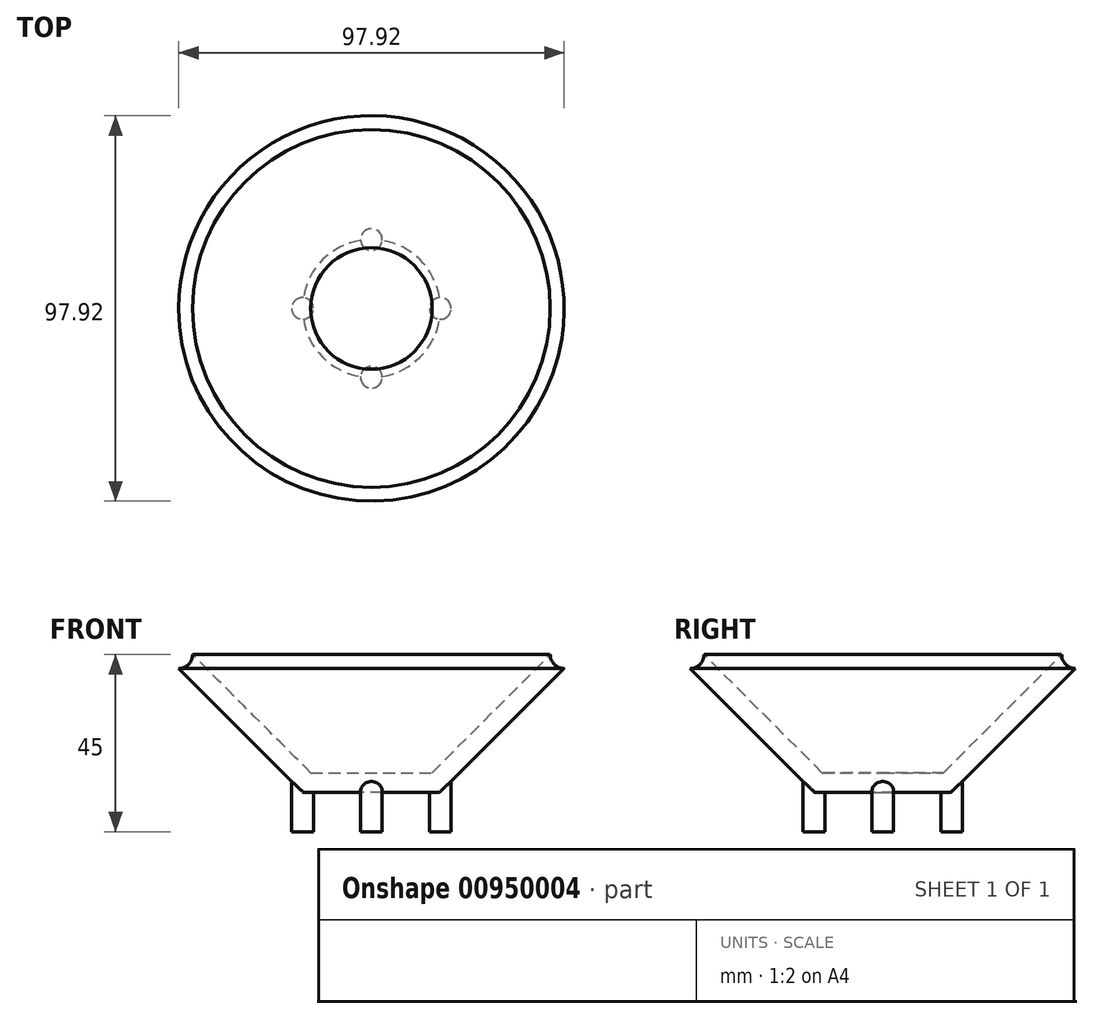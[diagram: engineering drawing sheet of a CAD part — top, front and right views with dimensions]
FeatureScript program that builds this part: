
annotation { "Feature Type Name" : "Feature", "Feature Type Description" : "" }
export const myFeature = defineFeature(function(context is Context, id is Id, definition is map)
    precondition{}
    {
        {
            var Q0;
            Q0=qCreatedBy(makeId("Front.planeOp"),FACE);
            var sketch = newSketch(context, id + "F0", { "sketchPlane" : qUnion([Q0])});
            skLineSegment(sketch, "E0", {"start": v(0, 0) * mm, "end": v(0, 35) * mm, "construction": true});
            skLineSegment(sketch, "E1", {"start": v(0, 0) * mm, "end": v(17.5, 0) * mm});
            skLineSegment(sketch, "E2", {"start": v(17.5, 0) * mm, "end": v(52.5, 35) * mm});
            skLineSegment(sketch, "E3.0", {"start": v(15.43, 5) * mm, "end": v(45.43, 35) * mm});
            skLineSegment(sketch, "E3.1", {"start": v(0, 5) * mm, "end": v(15.43, 5) * mm});
            skLineSegment(sketch, "E4", {"start": v(0, 5) * mm, "end": v(0, 0) * mm});
            skLineSegment(sketch, "E5", {"start": v(45.43, 35) * mm, "end": v(52.5, 35) * mm});
            skCircle(sketch, "E6", {"center": v(48.96, 35) * mm, "radius": 3.54 * mm});
            skPoint(sketch, "E6.centerSnap0", {"position": v(48.96, 35) * mm});
            skLineSegment(sketch, "E7", {"start": v(52.5, 35) * mm, "end": v(45.43, 35) * mm});
            skSolve(sketch);
        }
        {
            var Q0;
            {var subQ2=sQuery(id+"F0.wireOp",EDGE,"E1");Q0=makeQuery(id+"F0.imprint","IMPRINT",FACE,{"disambiguationData":[TD([[makeQuery(id+"F0.imprint","IMPRINT",EDGE,{"derivedFrom":subQ2}),1.0]])]});}
            var Q1;
            {var subQ0=sQuery(id+"F0.wireOp",EDGE,"E7");Q1=makeQuery(id+"F0.imprint","IMPRINT",FACE,{"disambiguationData":[TD([[makeQuery(id+"F0.imprint","IMPRINT",EDGE,{"derivedFrom":subQ0}),-1.0]])]});}
            var Q2;
            {var subQ0=sQuery(id+"F0.wireOp",EDGE,"E7");Q2=makeQuery(id+"F0.imprint","IMPRINT",FACE,{"disambiguationData":[TD([[makeQuery(id+"F0.imprint","IMPRINT",EDGE,{"derivedFrom":subQ0}),1.0]])]});}
            var Q3;
            Q3=sQuery(id+"F0.wireOp",EDGE,"E0");
            revolve(context, id + "F1", {"surfaceOperationType" : NewSurfaceOperationType.NEW, "entities" : qUnion([Q0, Q1, Q2]), "axis" : qUnion([Q3]), "revolveType" : RevolveType.FULL});
        }
        {
            var Q0;
            Q0=makeQuery(id+"F1.opRevolve","SWEPT_FACE",FACE,{"disambiguationData":[OSD([sQuery(id+"F0.wireOp",EDGE,"E1")])]});
            var sketch = newSketch(context, id + "F2", { "sketchPlane" : qUnion([Q0])});
            skLineSegment(sketch, "E8", {"start": v(-50.3, 0) * mm, "end": v(49.89, 0) * mm, "construction": true});
            skLineSegment(sketch, "E9", {"start": v(0, 49.68) * mm, "end": v(0, -50.5) * mm, "construction": true});
            skCircle(sketch, "E10", {"center": v(17.5, 0) * mm, "radius": 2.75 * mm});
            skCircle(sketch, "E11", {"center": v(0, 17.5) * mm, "radius": 2.75 * mm});
            skCircle(sketch, "E12", {"center": v(-17.5, 0) * mm, "radius": 2.75 * mm});
            skCircle(sketch, "E13", {"center": v(0, -17.5) * mm, "radius": 2.75 * mm});
            skSolve(sketch);
        }
        {
            var Q0;
            {var subQ0=sQuery(id+"F2.wireOp",EDGE,"E12");var subQ1=makeQuery(id+"F1.opRevolve","SWEPT_EDGE",EDGE,{"disambiguationData":[OSD([sQuery(id+"F0.wireOp",EDGE,"E1"),sQuery(id+"F0.wireOp",EDGE,"E2")])]});var subQ2=makeQuery(id+"F2.imprint","INTERSECT",VERTEX,{"disambiguationData":[OD(0.0)],"derivedFrom":[subQ1,subQ0]});Q0=makeQuery(id+"F2.imprint","IMPRINT",FACE,{"disambiguationData":[TD([[makeQuery(id+"F2.imprint","IMPRINT",EDGE,{"disambiguationData":[TD([[subQ2,-1.0]])],"derivedFrom":subQ0}),1.0]])]});}
            var Q1;
            {var subQ0=sQuery(id+"F2.wireOp",EDGE,"E11");var subQ1=makeQuery(id+"F1.opRevolve","SWEPT_EDGE",EDGE,{"disambiguationData":[OSD([sQuery(id+"F0.wireOp",EDGE,"E1"),sQuery(id+"F0.wireOp",EDGE,"E2")])]});var subQ2=makeQuery(id+"F2.imprint","INTERSECT",VERTEX,{"disambiguationData":[OD(0.0)],"derivedFrom":[subQ1,subQ0]});Q1=makeQuery(id+"F2.imprint","IMPRINT",FACE,{"disambiguationData":[TD([[makeQuery(id+"F2.imprint","IMPRINT",EDGE,{"disambiguationData":[TD([[subQ2,1.0]])],"derivedFrom":subQ0}),1.0]])]});}
            var Q2;
            {var subQ0=sQuery(id+"F2.wireOp",EDGE,"E13");var subQ1=makeQuery(id+"F1.opRevolve","SWEPT_EDGE",EDGE,{"disambiguationData":[OSD([sQuery(id+"F0.wireOp",EDGE,"E1"),sQuery(id+"F0.wireOp",EDGE,"E2")])]});var subQ2=makeQuery(id+"F2.imprint","INTERSECT",VERTEX,{"disambiguationData":[OD(0.0)],"derivedFrom":[subQ1,subQ0]});Q2=makeQuery(id+"F2.imprint","IMPRINT",FACE,{"disambiguationData":[TD([[makeQuery(id+"F2.imprint","IMPRINT",EDGE,{"disambiguationData":[TD([[subQ2,-1.0]])],"derivedFrom":subQ0}),1.0]])]});}
            var Q3;
            {var subQ0=sQuery(id+"F2.wireOp",EDGE,"E10");var subQ1=makeQuery(id+"F1.opRevolve","SWEPT_EDGE",EDGE,{"disambiguationData":[OSD([sQuery(id+"F0.wireOp",EDGE,"E1"),sQuery(id+"F0.wireOp",EDGE,"E2")])]});var subQ2=makeQuery(id+"F2.imprint","INTERSECT",VERTEX,{"disambiguationData":[OD(0.0)],"derivedFrom":[subQ1,subQ0]});Q3=makeQuery(id+"F2.imprint","IMPRINT",FACE,{"disambiguationData":[TD([[makeQuery(id+"F2.imprint","IMPRINT",EDGE,{"disambiguationData":[TD([[subQ2,1.0]])],"derivedFrom":subQ0}),1.0]])]});}
            extrude(context, id + "F3", {"entities" : qUnion([Q0, Q1, Q2, Q3]), "operationType" : NewBodyOperationType.ADD, "endBound" : BoundingType.UP_TO_NEXT, "oppositeDirection" : true, "depth" : 25 * mm, "offsetDistance" : 25 * mm});
        }
        {
            var Q0;
            {var subQ0=sQuery(id+"F2.wireOp",EDGE,"E10");var subQ1=makeQuery(id+"F1.opRevolve","SWEPT_EDGE",EDGE,{"disambiguationData":[OSD([sQuery(id+"F0.wireOp",EDGE,"E1"),sQuery(id+"F0.wireOp",EDGE,"E2")])]});var subQ2=makeQuery(id+"F2.imprint","INTERSECT",VERTEX,{"disambiguationData":[OD(0.0)],"derivedFrom":[subQ1,subQ0]});Q0=makeQuery(id+"F2.imprint","IMPRINT",FACE,{"disambiguationData":[TD([[makeQuery(id+"F2.imprint","IMPRINT",EDGE,{"disambiguationData":[TD([[subQ2,1.0]])],"derivedFrom":subQ0}),1.0]])]});}
            var Q1;
            {var subQ0=sQuery(id+"F2.wireOp",EDGE,"E11");var subQ1=makeQuery(id+"F1.opRevolve","SWEPT_EDGE",EDGE,{"disambiguationData":[OSD([sQuery(id+"F0.wireOp",EDGE,"E1"),sQuery(id+"F0.wireOp",EDGE,"E2")])]});var subQ2=makeQuery(id+"F2.imprint","INTERSECT",VERTEX,{"disambiguationData":[OD(0.0)],"derivedFrom":[subQ1,subQ0]});Q1=makeQuery(id+"F2.imprint","IMPRINT",FACE,{"disambiguationData":[TD([[makeQuery(id+"F2.imprint","IMPRINT",EDGE,{"disambiguationData":[TD([[subQ2,1.0]])],"derivedFrom":subQ0}),1.0]])]});}
            var Q2;
            {var subQ0=sQuery(id+"F2.wireOp",EDGE,"E12");var subQ1=makeQuery(id+"F1.opRevolve","SWEPT_EDGE",EDGE,{"disambiguationData":[OSD([sQuery(id+"F0.wireOp",EDGE,"E1"),sQuery(id+"F0.wireOp",EDGE,"E2")])]});var subQ2=makeQuery(id+"F2.imprint","INTERSECT",VERTEX,{"disambiguationData":[OD(0.0)],"derivedFrom":[subQ1,subQ0]});Q2=makeQuery(id+"F2.imprint","IMPRINT",FACE,{"disambiguationData":[TD([[makeQuery(id+"F2.imprint","IMPRINT",EDGE,{"disambiguationData":[TD([[subQ2,-1.0]])],"derivedFrom":subQ0}),1.0]])]});}
            var Q3;
            {var subQ0=sQuery(id+"F2.wireOp",EDGE,"E13");var subQ1=makeQuery(id+"F1.opRevolve","SWEPT_EDGE",EDGE,{"disambiguationData":[OSD([sQuery(id+"F0.wireOp",EDGE,"E1"),sQuery(id+"F0.wireOp",EDGE,"E2")])]});var subQ2=makeQuery(id+"F2.imprint","INTERSECT",VERTEX,{"disambiguationData":[OD(0.0)],"derivedFrom":[subQ1,subQ0]});Q3=makeQuery(id+"F2.imprint","IMPRINT",FACE,{"disambiguationData":[TD([[makeQuery(id+"F2.imprint","IMPRINT",EDGE,{"disambiguationData":[TD([[subQ2,-1.0]])],"derivedFrom":subQ0}),1.0]])]});}
            var Q4;
            {var subQ0=sQuery(id+"F2.wireOp",EDGE,"E12");var subQ1=makeQuery(id+"F1.opRevolve","SWEPT_EDGE",EDGE,{"disambiguationData":[OSD([sQuery(id+"F0.wireOp",EDGE,"E1"),sQuery(id+"F0.wireOp",EDGE,"E2")])]});var subQ2=makeQuery(id+"F2.imprint","INTERSECT",VERTEX,{"disambiguationData":[OD(0.0)],"derivedFrom":[subQ1,subQ0]});Q4=makeQuery(id+"F2.imprint","IMPRINT",FACE,{"disambiguationData":[TD([[makeQuery(id+"F2.imprint","IMPRINT",EDGE,{"disambiguationData":[TD([[subQ2,1.0]])],"derivedFrom":subQ0}),1.0]])]});}
            var Q5;
            {var subQ0=sQuery(id+"F2.wireOp",EDGE,"E13");var subQ1=makeQuery(id+"F1.opRevolve","SWEPT_EDGE",EDGE,{"disambiguationData":[OSD([sQuery(id+"F0.wireOp",EDGE,"E1"),sQuery(id+"F0.wireOp",EDGE,"E2")])]});var subQ2=makeQuery(id+"F2.imprint","INTERSECT",VERTEX,{"disambiguationData":[OD(0.0)],"derivedFrom":[subQ1,subQ0]});Q5=makeQuery(id+"F2.imprint","IMPRINT",FACE,{"disambiguationData":[TD([[makeQuery(id+"F2.imprint","IMPRINT",EDGE,{"disambiguationData":[TD([[subQ2,1.0]])],"derivedFrom":subQ0}),1.0]])]});}
            var Q6;
            {var subQ0=sQuery(id+"F2.wireOp",EDGE,"E11");var subQ1=makeQuery(id+"F1.opRevolve","SWEPT_EDGE",EDGE,{"disambiguationData":[OSD([sQuery(id+"F0.wireOp",EDGE,"E1"),sQuery(id+"F0.wireOp",EDGE,"E2")])]});var subQ2=makeQuery(id+"F2.imprint","INTERSECT",VERTEX,{"disambiguationData":[OD(0.0)],"derivedFrom":[subQ1,subQ0]});Q6=makeQuery(id+"F2.imprint","IMPRINT",FACE,{"disambiguationData":[TD([[makeQuery(id+"F2.imprint","IMPRINT",EDGE,{"disambiguationData":[TD([[subQ2,-1.0]])],"derivedFrom":subQ0}),1.0]])]});}
            var Q7;
            {var subQ0=sQuery(id+"F2.wireOp",EDGE,"E10");var subQ1=makeQuery(id+"F1.opRevolve","SWEPT_EDGE",EDGE,{"disambiguationData":[OSD([sQuery(id+"F0.wireOp",EDGE,"E1"),sQuery(id+"F0.wireOp",EDGE,"E2")])]});var subQ2=makeQuery(id+"F2.imprint","INTERSECT",VERTEX,{"disambiguationData":[OD(0.0)],"derivedFrom":[subQ1,subQ0]});Q7=makeQuery(id+"F2.imprint","IMPRINT",FACE,{"disambiguationData":[TD([[makeQuery(id+"F2.imprint","IMPRINT",EDGE,{"disambiguationData":[TD([[subQ2,-1.0]])],"derivedFrom":subQ0}),1.0]])]});}
            extrude(context, id + "F4", {"entities" : qUnion([Q0, Q1, Q2, Q3, Q4, Q5, Q6, Q7]), "operationType" : NewBodyOperationType.ADD, "depth" : 10 * mm, "offsetDistance" : 25 * mm});
        }
    });
